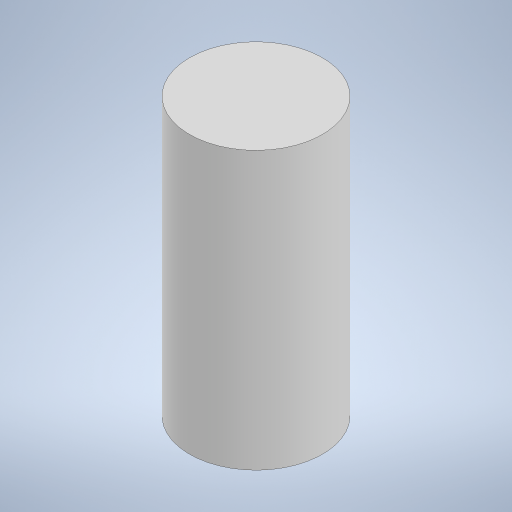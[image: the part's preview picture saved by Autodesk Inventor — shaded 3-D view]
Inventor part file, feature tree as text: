
AUTODESK INVENTOR PART (.ipt)
format: ipt  version: 2023 (Build 270158000, 158)  size: 198,656 bytes
history: native  units: in
note: dims shown in document units (in); Inventor stores cm internally (conversion verified against a paired STEP export)
features: extrude x1, sketch x1
ambient origin geometry x8: Origin, YZ Plane, XZ Plane, XY Plane, X Axis, Y Axis, Z Axis, Center Point
bodies: Solid1 (feature_tree)
feature tree (2):
  extrude  "Extrusion1"  Depth=0.5in TaperAngle=0.0deg
  sketch  "Sketch1"  dims[d0=0.24in d1=0.5in d2=0.0in]
